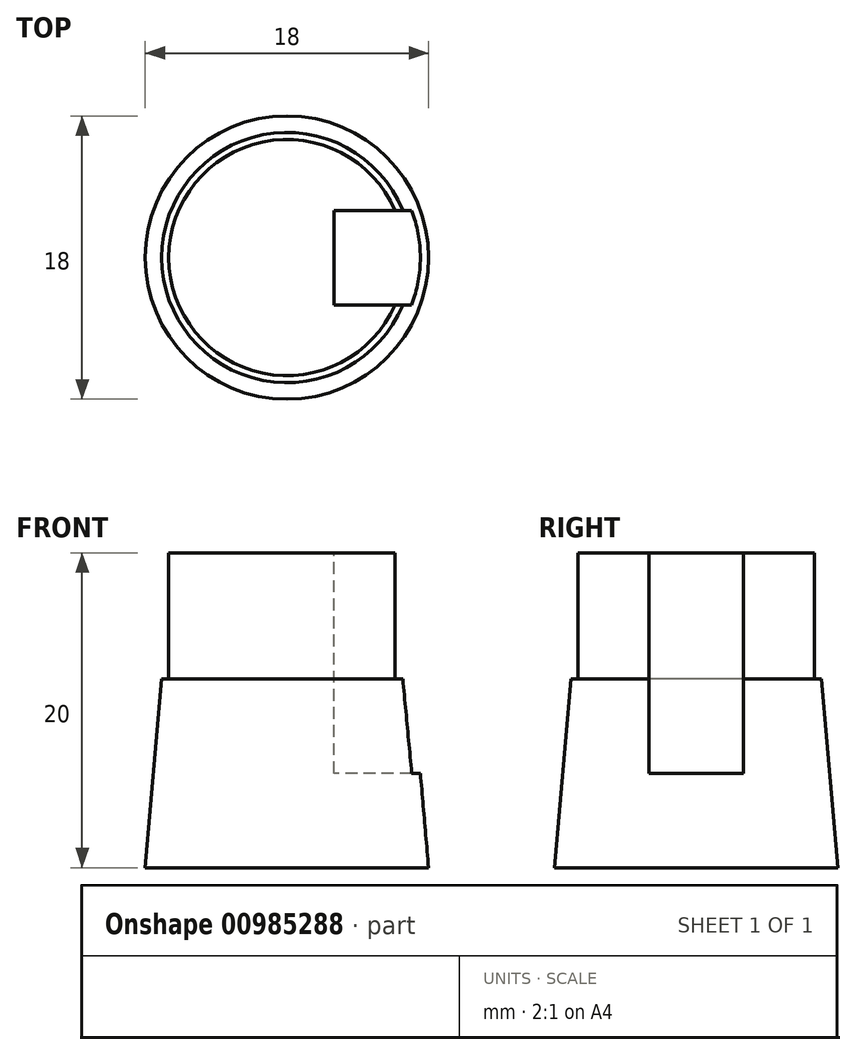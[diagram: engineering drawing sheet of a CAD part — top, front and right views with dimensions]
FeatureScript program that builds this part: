
annotation { "Feature Type Name" : "Feature", "Feature Type Description" : "" }
export const myFeature = defineFeature(function(context is Context, id is Id, definition is map)
    precondition{}
    {
        {
            var Q0;
            Q0=qCreatedBy(makeId("Top.planeOp"),FACE);
            var sketch = newSketch(context, id + "F0", { "sketchPlane" : qUnion([Q0])});
            skCircle(sketch, "E0", {"center": v(0, 0) * mm, "radius": 9 * mm});
            skSolve(sketch);
        }
        {
            var Q0;
            Q0=makeQuery(id+"F0.imprint","IMPRINT",FACE,{"disambiguationData":[TD([[makeQuery(id+"F0.imprint","IMPRINT",EDGE,{"derivedFrom":sQuery(id+"F0.wireOp",EDGE,"E0")}),1.0]])]});
            extrude(context, id + "F1", {"entities" : qUnion([Q0]), "depth" : 20 * mm, "offsetDistance" : 25 * mm, "hasDraft" : true, "draftAngle" : 5 * degree, "draftPullDirection" : true});
        }
        {
            var Q0;
            Q0=makeQuery(id+"F1.opExtrude","CAP_FACE",FACE,{"disambiguationData":[OSD([sQuery(id+"F0.wireOp",EDGE,"E0")])],"isStart":false});
            var sketch = newSketch(context, id + "F2", { "sketchPlane" : qUnion([Q0])});
            skCircle(sketch, "E1.0", {"center": v(0, 0) * mm, "radius": 7.25 * mm});
            skCircle(sketch, "E2", {"center": v(0, 0) * mm, "radius": 7.5 * mm});
            skSolve(sketch);
        }
        {
            var Q0;
            Q0=makeQuery(id+"F2.imprint","IMPRINT",FACE,{"disambiguationData":[TD([[makeQuery(id+"F2.imprint","IMPRINT",EDGE,{"derivedFrom":sQuery(id+"F2.wireOp",EDGE,"E1.0")}),-1.0]])]});
            extrude(context, id + "F3", {"entities" : qUnion([Q0]), "operationType" : NewBodyOperationType.ADD, "oppositeDirection" : true, "depth" : 10 * mm, "offsetDistance" : 25 * mm});
        }
        {
            var Q0;
            Q0=makeQuery(id+"F3.boolean.opBoolean","MERGE",FACE,{"derivedFrom":[makeQuery(id+"F1.opExtrude","CAP_FACE",FACE,{"disambiguationData":[OSD([sQuery(id+"F0.wireOp",EDGE,"E0")])],"isStart":false}),makeQuery(id+"F3.opExtrude","CAP_FACE",FACE,{"disambiguationData":[OSD([sQuery(id+"F2.wireOp",EDGE,"E1.0"),sQuery(id+"F2.wireOp",EDGE,"E2")])],"isStart":true})]});
            var sketch = newSketch(context, id + "F4", { "sketchPlane" : qUnion([Q0])});
            skCircle(sketch, "E3.0", {"center": v(0, 0) * mm, "radius": 7.5 * mm});
            skCircle(sketch, "E4.0", {"center": v(0, 0) * mm, "radius": 9 * mm});
            skSolve(sketch);
        }
        {
            var Q0;
            Q0=makeQuery(id+"F4.imprint","IMPRINT",FACE,{"disambiguationData":[TD([[makeQuery(id+"F4.imprint","IMPRINT",EDGE,{"derivedFrom":sQuery(id+"F4.wireOp",EDGE,"E3.0")}),-1.0]])]});
            extrude(context, id + "F5", {"entities" : qUnion([Q0]), "operationType" : NewBodyOperationType.REMOVE, "oppositeDirection" : true, "depth" : 8 * mm, "offsetDistance" : 25 * mm});
        }
        {
            var Q0;
            Q0=makeQuery(id+"F3.boolean.opBoolean","MERGE",FACE,{"derivedFrom":[makeQuery(id+"F1.opExtrude","CAP_FACE",FACE,{"disambiguationData":[OSD([sQuery(id+"F0.wireOp",EDGE,"E0")])],"isStart":false}),makeQuery(id+"F3.opExtrude","CAP_FACE",FACE,{"disambiguationData":[OSD([sQuery(id+"F2.wireOp",EDGE,"E1.0"),sQuery(id+"F2.wireOp",EDGE,"E2")])],"isStart":true})]});
            var sketch = newSketch(context, id + "F6", { "sketchPlane" : qUnion([Q0])});
            skLineSegment(sketch, "E5.bottom", {"start": v(9, -3) * mm, "end": v(3, -3) * mm});
            skLineSegment(sketch, "E5.top", {"start": v(9, 3) * mm, "end": v(3, 3) * mm});
            skLineSegment(sketch, "E5.left", {"start": v(9, -3) * mm, "end": v(9, 3) * mm});
            skLineSegment(sketch, "E5.right", {"start": v(3, -3) * mm, "end": v(3, 3) * mm});
            skSolve(sketch);
        }
        {
            var Q0;
            {var subQ0=sQuery(id+"F6.wireOp",EDGE,"E5.left");Q0=makeQuery(id+"F6.imprint","IMPRINT",FACE,{"disambiguationData":[TD([[makeQuery(id+"F6.imprint","IMPRINT",EDGE,{"derivedFrom":subQ0}),1.0]])]});}
            var Q1;
            {var subQ0=sQuery(id+"F6.wireOp",EDGE,"E5.right");Q1=makeQuery(id+"F6.imprint","IMPRINT",FACE,{"disambiguationData":[TD([[makeQuery(id+"F6.imprint","IMPRINT",EDGE,{"derivedFrom":subQ0}),-1.0]])]});}
            extrude(context, id + "F7", {"entities" : qUnion([Q0, Q1]), "operationType" : NewBodyOperationType.REMOVE, "oppositeDirection" : true, "depth" : 14 * mm, "offsetDistance" : 25 * mm});
        }
    });
